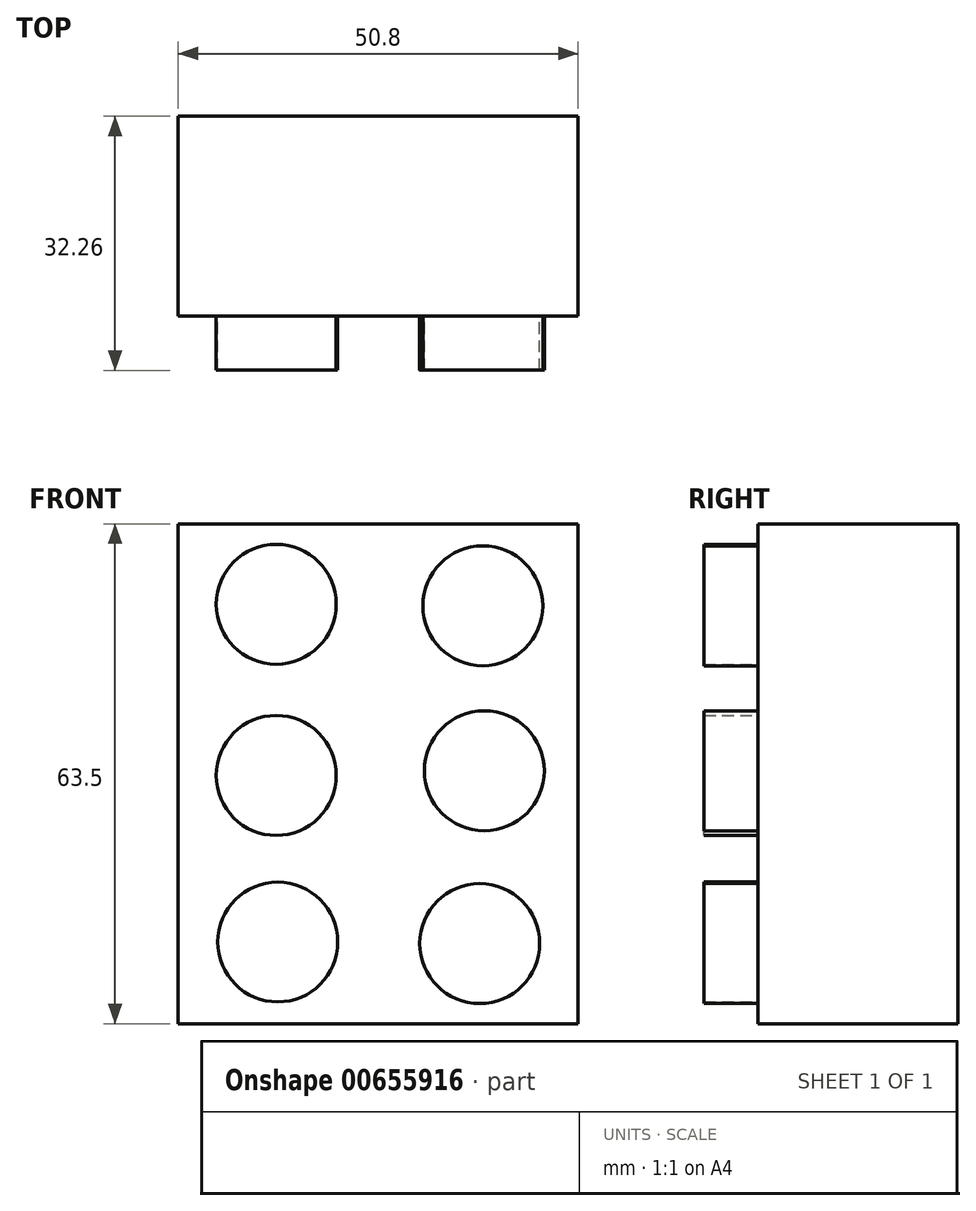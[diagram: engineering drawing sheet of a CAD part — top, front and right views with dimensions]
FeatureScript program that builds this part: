
annotation { "Feature Type Name" : "Feature", "Feature Type Description" : "" }
export const myFeature = defineFeature(function(context is Context, id is Id, definition is map)
    precondition{}
    {
        {
            var Q0;
            Q0=qCreatedBy(makeId("Origin.pointOp"),VERTEX);
            var Q1;
            Q1=qCreatedBy(makeId("Top.planeOp"),FACE);
            cPlane(context, id + "F0", {"entities" : qUnion([Q0, Q1]), "cplaneType" : CPlaneType.PLANE_POINT, "offset" : 25.4 * mm, "width" : 152.4 * mm, "height" : 152.4 * mm});
        }
        {
            var Q0;
            Q0=qCreatedBy(makeId("Top.planeOp"),FACE);
            var sketch = newSketch(context, id + "F1", { "sketchPlane" : qUnion([Q0])});
            skLineSegment(sketch, "E0.bottom", {"start": v(0, 0) * mm, "end": v(-50.8, 0) * mm});
            skLineSegment(sketch, "E0.top", {"start": v(0, 25.4) * mm, "end": v(-50.8, 25.4) * mm});
            skLineSegment(sketch, "E0.left", {"start": v(0, 0) * mm, "end": v(0, 25.4) * mm});
            skLineSegment(sketch, "E0.right", {"start": v(-50.8, 0) * mm, "end": v(-50.8, 25.4) * mm});
            skSolve(sketch);
        }
        {
            var Q0;
            Q0=makeQuery(id+"F1.imprint","IMPRINT",FACE,{"disambiguationData":[TD([[makeQuery(id+"F1.imprint","IMPRINT",EDGE,{"derivedFrom":sQuery(id+"F1.wireOp",EDGE,"E0.bottom")}),-1.0]])]});
            extrude(context, id + "F2", {"entities" : qUnion([Q0]), "depth" : 63.5 * mm, "offsetDistance" : 25.4 * mm});
        }
        {
            var Q0;
            Q0=makeQuery(id+"F2.opExtrude","SWEPT_FACE",FACE,{"disambiguationData":[OSD([sQuery(id+"F1.wireOp",EDGE,"E0.bottom")])]});
            var sketch = newSketch(context, id + "F3", { "sketchPlane" : qUnion([Q0])});
            skLineSegment(sketch, "E1", {"start": v(-25.4, 63.5) * mm, "end": v(-25.4, 0) * mm});
            skLineSegment(sketch, "E2", {"start": v(-50.8, 42.34) * mm, "end": v(0, 42.34) * mm});
            skLineSegment(sketch, "E3", {"start": v(-50.8, 21.19) * mm, "end": v(0, 21.19) * mm});
            skCircle(sketch, "E4", {"center": v(-38.35, 53.27) * mm, "radius": 7.62 * mm});
            skCircle(sketch, "E5", {"center": v(-12.1, 53.08) * mm, "radius": 7.62 * mm});
            skCircle(sketch, "E6", {"center": v(-38.35, 31.53) * mm, "radius": 7.62 * mm});
            skCircle(sketch, "E7", {"center": v(-38.15, 10.38) * mm, "radius": 7.62 * mm});
            skCircle(sketch, "E8", {"center": v(-11.9, 32.12) * mm, "radius": 7.62 * mm});
            skCircle(sketch, "E9", {"center": v(-12.5, 10.18) * mm, "radius": 7.62 * mm});
            skSolve(sketch);
        }
        {
            var Q0;
            Q0=makeQuery(id+"F3.imprint","IMPRINT",FACE,{"disambiguationData":[TD([[makeQuery(id+"F3.imprint","IMPRINT",EDGE,{"derivedFrom":sQuery(id+"F3.wireOp",EDGE,"E5")}),1.0]])]});
            var Q1;
            Q1=makeQuery(id+"F3.imprint","IMPRINT",FACE,{"disambiguationData":[TD([[makeQuery(id+"F3.imprint","IMPRINT",EDGE,{"derivedFrom":sQuery(id+"F3.wireOp",EDGE,"E4")}),1.0]])]});
            var Q2;
            Q2=makeQuery(id+"F3.imprint","IMPRINT",FACE,{"disambiguationData":[TD([[makeQuery(id+"F3.imprint","IMPRINT",EDGE,{"derivedFrom":sQuery(id+"F3.wireOp",EDGE,"E6")}),1.0]])]});
            var Q3;
            Q3=makeQuery(id+"F3.imprint","IMPRINT",FACE,{"disambiguationData":[TD([[makeQuery(id+"F3.imprint","IMPRINT",EDGE,{"derivedFrom":sQuery(id+"F3.wireOp",EDGE,"E8")}),1.0]])]});
            var Q4;
            Q4=makeQuery(id+"F3.imprint","IMPRINT",FACE,{"disambiguationData":[TD([[makeQuery(id+"F3.imprint","IMPRINT",EDGE,{"derivedFrom":sQuery(id+"F3.wireOp",EDGE,"E7")}),1.0]])]});
            var Q5;
            Q5=makeQuery(id+"F3.imprint","IMPRINT",FACE,{"disambiguationData":[TD([[makeQuery(id+"F3.imprint","IMPRINT",EDGE,{"derivedFrom":sQuery(id+"F3.wireOp",EDGE,"E9")}),1.0]])]});
            extrude(context, id + "F4", {"entities" : qUnion([Q0, Q1, Q2, Q3, Q4, Q5]), "operationType" : NewBodyOperationType.ADD, "depth" : 6.86 * mm, "offsetDistance" : 25.4 * mm});
        }
    });
